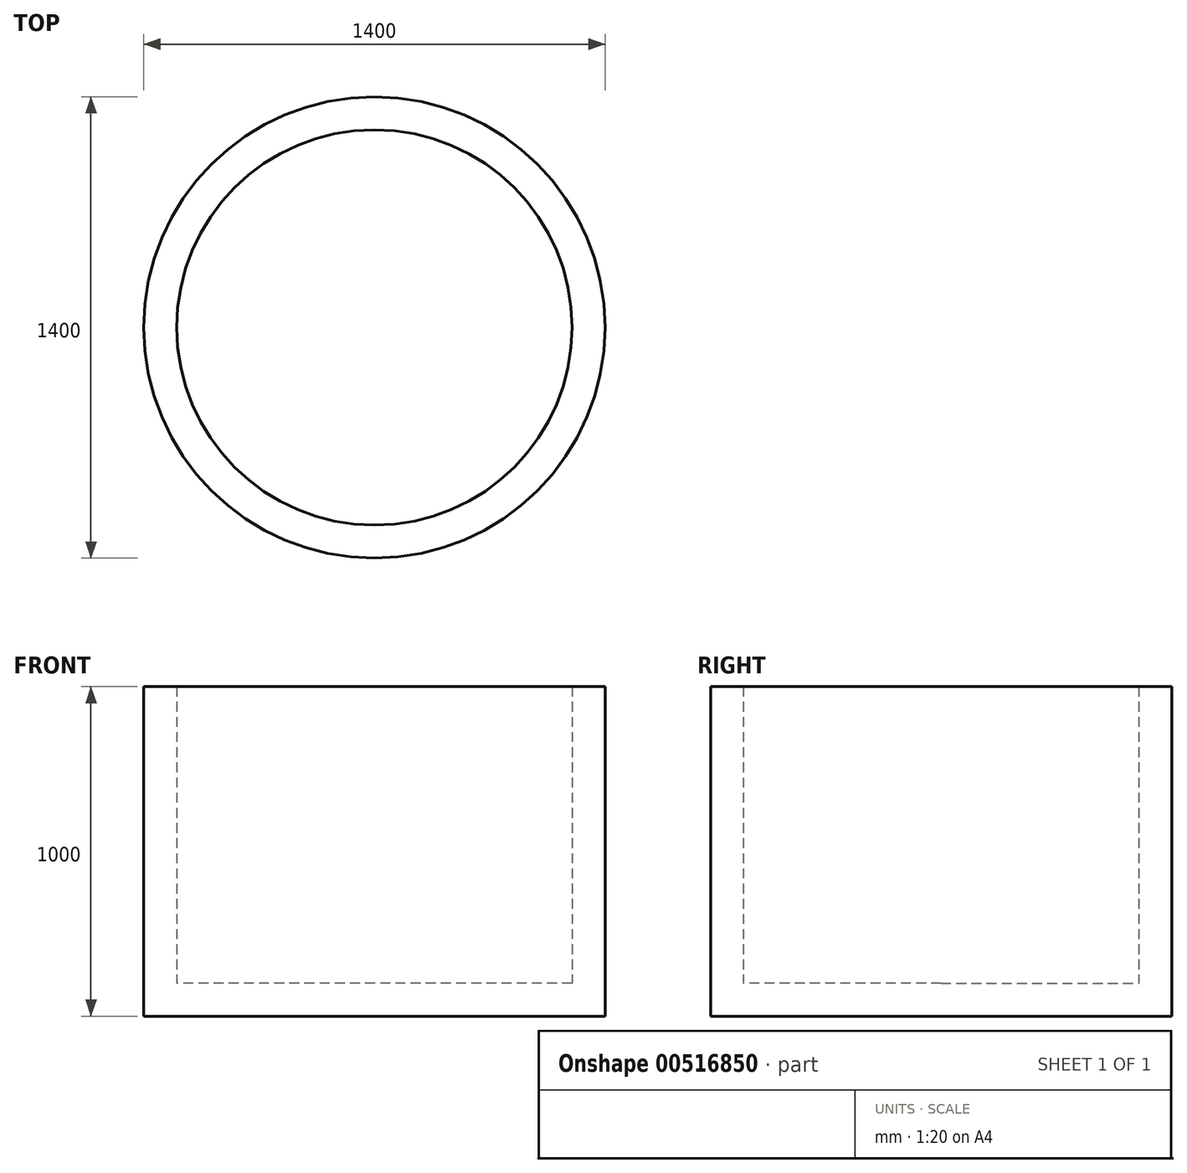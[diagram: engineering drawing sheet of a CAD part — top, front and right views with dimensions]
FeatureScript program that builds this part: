
annotation { "Feature Type Name" : "Feature", "Feature Type Description" : "" }
export const myFeature = defineFeature(function(context is Context, id is Id, definition is map)
    precondition{}
    {
        {
            var Q0;
            Q0=qCreatedBy(makeId("Top.planeOp"),FACE);
            var sketch = newSketch(context, id + "F0", { "sketchPlane" : qUnion([Q0])});
            skCircle(sketch, "E0", {"center": v(0, 0) * mm, "radius": 700 * mm});
            skSolve(sketch);
        }
        {
            var Q0;
            Q0=makeQuery(id+"F0.imprint","IMPRINT",FACE,{"disambiguationData":[TD([[makeQuery(id+"F0.imprint","IMPRINT",EDGE,{"derivedFrom":sQuery(id+"F0.wireOp",EDGE,"E0")}),1.0]])]});
            extrude(context, id + "F1", {"entities" : qUnion([Q0]), "endBound" : BoundingType.SYMMETRIC, "depth" : 100 * mm});
        }
        {
            var Q0;
            Q0=makeQuery(id+"F1.opExtrude","CAP_FACE",FACE,{"disambiguationData":[OSD([sQuery(id+"F0.wireOp",EDGE,"E0")])],"isStart":true});
            var sketch = newSketch(context, id + "F2", { "sketchPlane" : qUnion([Q0])});
            skCircle(sketch, "E1.0.0", {"center": v(0, 0) * mm, "radius": 700 * mm});
            skCircle(sketch, "E2", {"center": v(0, 0) * mm, "radius": 600 * mm});
            skSolve(sketch);
        }
        {
            var Q0;
            Q0=makeQuery(id+"F2.imprint","IMPRINT",FACE,{"disambiguationData":[TD([[makeQuery(id+"F2.imprint","IMPRINT",EDGE,{"derivedFrom":sQuery(id+"F2.wireOp",EDGE,"E1.0.0")}),-1.0]])]});
            extrude(context, id + "F3", {"entities" : qUnion([Q0]), "operationType" : NewBodyOperationType.ADD, "oppositeDirection" : true, "depth" : 1000 * mm});
        }
        {
            var Q0;
            Q0=qCreatedBy(makeId("Front.planeOp"),FACE);
            cPlane(context, id + "F4", {"entities" : qUnion([Q0]), "cplaneType" : CPlaneType.OFFSET, "offset" : 100 * mm, "width" : 150 * mm, "height" : 150 * mm});
        }
        {
            var Q0;
            Q0=qCreatedBy(id+"F4.planeOp",FACE);
            var sketch = newSketch(context, id + "F5", { "sketchPlane" : qUnion([Q0])});
            skLineSegment(sketch, "E3", {"start": v(-798.13, 146.53) * mm, "end": v(1436.35, 146.53) * mm, "construction": true});
            skSolve(sketch);
        }
        {
            var Q0;
            Q0=sQuery(id+"F5.wireOp",EDGE,"E3");
            cPlane(context, id + "F6", {"entities" : qUnion([Q0]), "cplaneType" : CPlaneType.LINE_ANGLE, "offset" : 25 * mm, "angle" : 45 * degree, "width" : 150 * mm, "height" : 150 * mm});
        }
    });
